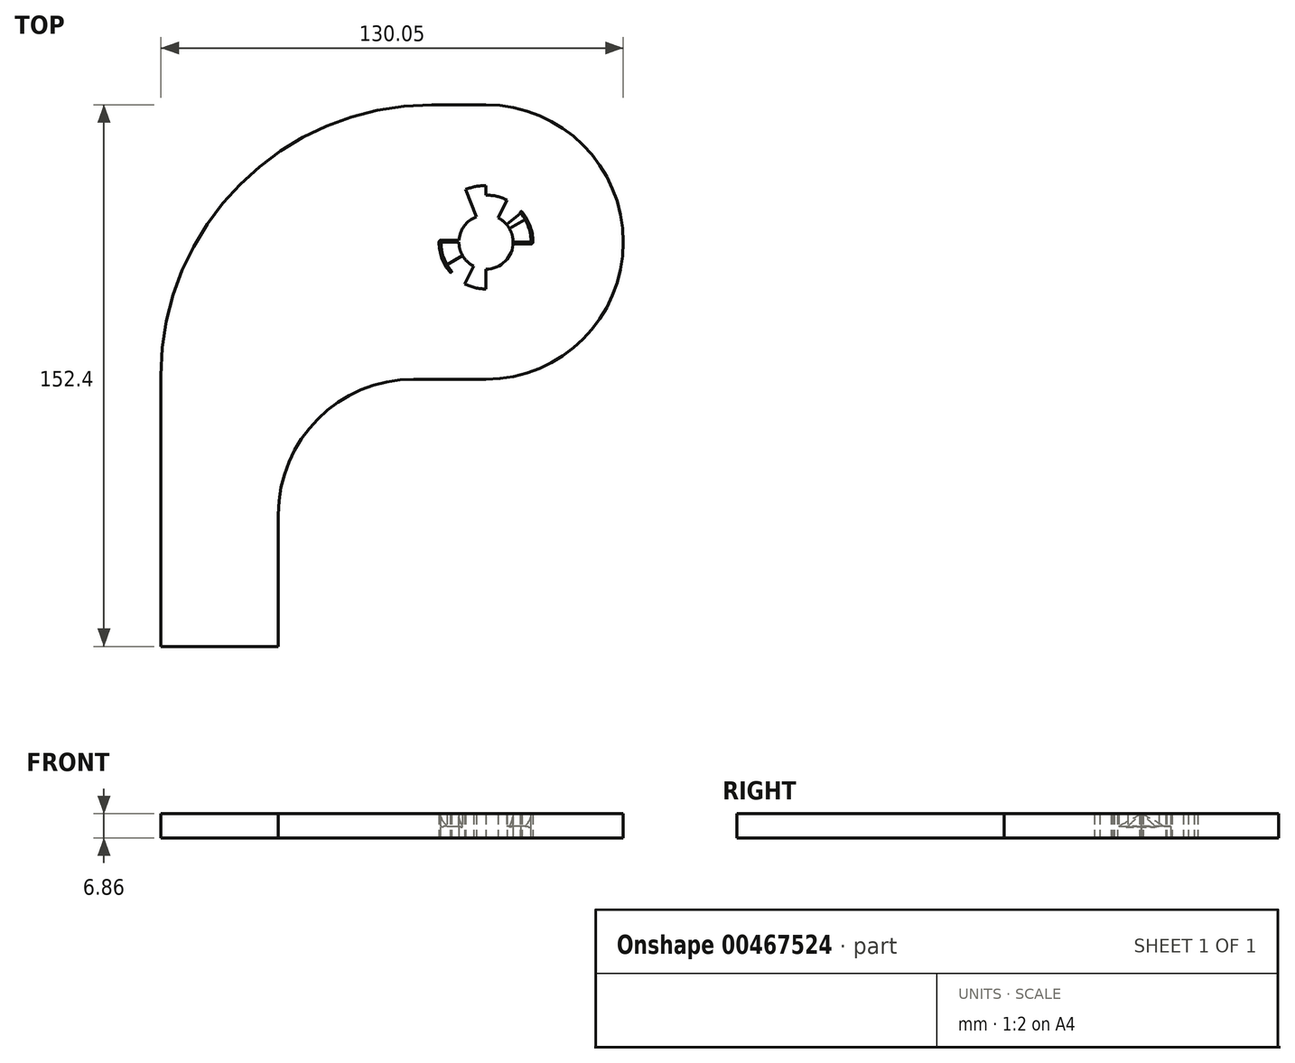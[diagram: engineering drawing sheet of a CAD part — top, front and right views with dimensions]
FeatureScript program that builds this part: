
annotation { "Feature Type Name" : "Feature", "Feature Type Description" : "" }
export const myFeature = defineFeature(function(context is Context, id is Id, definition is map)
    precondition{}
    {
        {
            var Q0;
            Q0=qCreatedBy(makeId("Front.planeOp"),FACE);
            var sketch = newSketch(context, id + "F0", { "sketchPlane" : qUnion([Q0])});
            skLineSegment(sketch, "E0", {"start": v(0, 0) * mm, "end": v(0, 25.4) * mm, "construction": true});
            skSolve(sketch);
        }
        {
            var Q0;
            Q0=qCreatedBy(makeId("Front.planeOp"),FACE);
            var Q1;
            Q1=sQuery(id+"F0.wireOp",EDGE,"E0");
            cPlane(context, id + "F1", {"entities" : qUnion([Q0, Q1]), "cplaneType" : CPlaneType.LINE_ANGLE, "offset" : 25.4 * mm, "angle" : 10 * degree, "width" : 152.4 * mm, "height" : 152.4 * mm});
        }
        {
            var Q0;
            Q0=qCreatedBy(makeId("Front.planeOp"),FACE);
            var Q1;
            Q1=sQuery(id+"F0.wireOp",EDGE,"E0");
            cPlane(context, id + "F2", {"entities" : qUnion([Q0, Q1]), "cplaneType" : CPlaneType.LINE_ANGLE, "offset" : 25.4 * mm, "angle" : 20 * degree, "width" : 152.4 * mm, "height" : 152.4 * mm});
        }
        {
            var Q0;
            Q0=qCreatedBy(makeId("Front.planeOp"),FACE);
            var Q1;
            Q1=sQuery(id+"F0.wireOp",EDGE,"E0");
            cPlane(context, id + "F3", {"entities" : qUnion([Q0, Q1]), "cplaneType" : CPlaneType.LINE_ANGLE, "offset" : 25.4 * mm, "angle" : 30 * degree, "width" : 152.4 * mm, "height" : 152.4 * mm});
        }
        {
            var Q0;
            Q0=qCreatedBy(makeId("Front.planeOp"),FACE);
            var sketch = newSketch(context, id + "F4", { "sketchPlane" : qUnion([Q0])});
            skLineSegment(sketch, "E1", {"start": v(0, 0) * mm, "end": v(-12.7, 0) * mm, "construction": true});
            skLineSegment(sketch, "E2.bottom", {"start": v(-12.7, 0) * mm, "end": v(-7.62, 0) * mm});
            skLineSegment(sketch, "E2.top", {"start": v(-12.7, 3.76) * mm, "end": v(-7.62, 3.76) * mm});
            skLineSegment(sketch, "E2.left", {"start": v(-12.7, 0) * mm, "end": v(-12.7, 3.76) * mm});
            skLineSegment(sketch, "E2.right", {"start": v(-7.62, 0) * mm, "end": v(-7.62, 3.76) * mm});
            skSolve(sketch);
        }
        {
            var Q0;
            Q0=qCreatedBy(id+"F1.planeOp",FACE);
            var sketch = newSketch(context, id + "F5", { "sketchPlane" : qUnion([Q0])});
            skLineSegment(sketch, "E3", {"start": v(0, 0) * mm, "end": v(12.7, 0) * mm, "construction": true});
            skLineSegment(sketch, "E4.bottom", {"start": v(12.7, 0) * mm, "end": v(7.62, 0) * mm});
            skLineSegment(sketch, "E4.top", {"start": v(12.7, 2.6) * mm, "end": v(7.62, 2.6) * mm});
            skLineSegment(sketch, "E4.left", {"start": v(12.7, 0) * mm, "end": v(12.7, 2.6) * mm});
            skLineSegment(sketch, "E4.right", {"start": v(7.62, 0) * mm, "end": v(7.62, 2.6) * mm});
            skSolve(sketch);
        }
        {
            var Q0;
            Q0=qCreatedBy(id+"F2.planeOp",FACE);
            var sketch = newSketch(context, id + "F6", { "sketchPlane" : qUnion([Q0])});
            skLineSegment(sketch, "E5", {"start": v(0, 0) * mm, "end": v(12.7, 0) * mm, "construction": true});
            skLineSegment(sketch, "E6.bottom", {"start": v(12.7, 0) * mm, "end": v(7.62, 0) * mm});
            skLineSegment(sketch, "E6.top", {"start": v(12.7, 1.42) * mm, "end": v(7.62, 1.42) * mm});
            skLineSegment(sketch, "E6.left", {"start": v(12.7, 0) * mm, "end": v(12.7, 1.42) * mm});
            skLineSegment(sketch, "E6.right", {"start": v(7.62, 0) * mm, "end": v(7.62, 1.42) * mm});
            skSolve(sketch);
        }
        {
            var Q0;
            Q0=qCreatedBy(id+"F3.planeOp",FACE);
            var sketch = newSketch(context, id + "F7", { "sketchPlane" : qUnion([Q0])});
            skLineSegment(sketch, "E7", {"start": v(0, 0) * mm, "end": v(12.7, 0) * mm, "construction": true});
            skLineSegment(sketch, "E8.bottom", {"start": v(12.7, 0) * mm, "end": v(7.62, 0) * mm});
            skLineSegment(sketch, "E8.top", {"start": v(12.7, 0.25) * mm, "end": v(7.62, 0.25) * mm});
            skLineSegment(sketch, "E8.left", {"start": v(12.7, 0) * mm, "end": v(12.7, 0.25) * mm});
            skLineSegment(sketch, "E8.right", {"start": v(7.62, 0) * mm, "end": v(7.62, 0.25) * mm});
            skLineSegment(sketch, "E9", {"start": v(0, 0) * mm, "end": v(-12.7, 0) * mm, "construction": true});
            skLineSegment(sketch, "E10.bottom", {"start": v(-12.7, 0) * mm, "end": v(-7.62, 0) * mm});
            skLineSegment(sketch, "E10.top", {"start": v(-12.7, 0.25) * mm, "end": v(-7.62, 0.25) * mm});
            skLineSegment(sketch, "E10.left", {"start": v(-12.7, 0) * mm, "end": v(-12.7, 0.25) * mm});
            skLineSegment(sketch, "E10.right", {"start": v(-7.62, 0) * mm, "end": v(-7.62, 0.25) * mm});
            skSolve(sketch);
        }
        {
            var Q0;
            Q0=makeQuery(id+"F7.imprint","IMPRINT",FACE,{"disambiguationData":[TD([[makeQuery(id+"F7.imprint","IMPRINT",EDGE,{"derivedFrom":sQuery(id+"F7.wireOp",EDGE,"E8.bottom")}),-1.0]])]});
            var Q1;
            Q1=makeQuery(id+"F6.imprint","IMPRINT",FACE,{"disambiguationData":[TD([[makeQuery(id+"F6.imprint","IMPRINT",EDGE,{"derivedFrom":sQuery(id+"F6.wireOp",EDGE,"E6.bottom")}),-1.0]])]});
            var Q2;
            Q2=makeQuery(id+"F5.imprint","IMPRINT",FACE,{"disambiguationData":[TD([[makeQuery(id+"F5.imprint","IMPRINT",EDGE,{"derivedFrom":sQuery(id+"F5.wireOp",EDGE,"E4.bottom")}),-1.0]])]});
            var Q3;
            Q3=makeQuery(id+"F4.imprint","IMPRINT",FACE,{"disambiguationData":[TD([[makeQuery(id+"F4.imprint","IMPRINT",EDGE,{"derivedFrom":sQuery(id+"F4.wireOp",EDGE,"E2.bottom")}),1.0]])]});
            loft(context, id + "F8", {"sheetProfilesArray" : [{ "sheetProfileEntities" : qUnion([Q0]) }, { "sheetProfileEntities" : qUnion([Q1]) }, { "sheetProfileEntities" : qUnion([Q2]) }, { "sheetProfileEntities" : qUnion([Q3]) }]});
        }
        {
            var Q0;
            Q0=qCreatedBy(id+"F2.planeOp",FACE);
            var sketch = newSketch(context, id + "F9", { "sketchPlane" : qUnion([Q0])});
            skLineSegment(sketch, "E11", {"start": v(0, 0) * mm, "end": v(-12.7, 0) * mm, "construction": true});
            skLineSegment(sketch, "E12.bottom", {"start": v(-12.7, 0) * mm, "end": v(-7.62, 0) * mm});
            skLineSegment(sketch, "E12.top", {"start": v(-12.7, 1.42) * mm, "end": v(-7.62, 1.42) * mm});
            skLineSegment(sketch, "E12.left", {"start": v(-12.7, 0) * mm, "end": v(-12.7, 1.42) * mm});
            skLineSegment(sketch, "E12.right", {"start": v(-7.62, 0) * mm, "end": v(-7.62, 1.42) * mm});
            skSolve(sketch);
        }
        {
            var Q0;
            Q0=qCreatedBy(id+"F1.planeOp",FACE);
            var sketch = newSketch(context, id + "F10", { "sketchPlane" : qUnion([Q0])});
            skLineSegment(sketch, "E13", {"start": v(0, 0) * mm, "end": v(-12.7, 0) * mm, "construction": true});
            skLineSegment(sketch, "E14.bottom", {"start": v(-12.7, 0) * mm, "end": v(-7.62, 0) * mm});
            skLineSegment(sketch, "E14.top", {"start": v(-12.7, 2.6) * mm, "end": v(-7.62, 2.6) * mm});
            skLineSegment(sketch, "E14.left", {"start": v(-12.7, 0) * mm, "end": v(-12.7, 2.6) * mm});
            skLineSegment(sketch, "E14.right", {"start": v(-7.62, 0) * mm, "end": v(-7.62, 2.6) * mm});
            skSolve(sketch);
        }
        {
            var Q0;
            Q0=qCreatedBy(makeId("Front.planeOp"),FACE);
            var sketch = newSketch(context, id + "F11", { "sketchPlane" : qUnion([Q0])});
            skLineSegment(sketch, "E15", {"start": v(0, 0) * mm, "end": v(12.7, 0) * mm, "construction": true});
            skLineSegment(sketch, "E16.bottom", {"start": v(12.7, 0) * mm, "end": v(7.62, 0) * mm});
            skLineSegment(sketch, "E16.top", {"start": v(12.7, 3.76) * mm, "end": v(7.62, 3.76) * mm});
            skLineSegment(sketch, "E16.left", {"start": v(12.7, 0) * mm, "end": v(12.7, 3.76) * mm});
            skLineSegment(sketch, "E16.right", {"start": v(7.62, 0) * mm, "end": v(7.62, 3.76) * mm});
            skSolve(sketch);
        }
        {
            var Q0;
            Q0=makeQuery(id+"F7.imprint","IMPRINT",FACE,{"disambiguationData":[TD([[makeQuery(id+"F7.imprint","IMPRINT",EDGE,{"derivedFrom":sQuery(id+"F7.wireOp",EDGE,"E10.bottom")}),1.0]])]});
            var Q1;
            Q1=makeQuery(id+"F9.imprint","IMPRINT",FACE,{"disambiguationData":[TD([[makeQuery(id+"F9.imprint","IMPRINT",EDGE,{"derivedFrom":sQuery(id+"F9.wireOp",EDGE,"E12.bottom")}),1.0]])]});
            var Q2;
            Q2=makeQuery(id+"F10.imprint","IMPRINT",FACE,{"disambiguationData":[TD([[makeQuery(id+"F10.imprint","IMPRINT",EDGE,{"derivedFrom":sQuery(id+"F10.wireOp",EDGE,"E14.bottom")}),1.0]])]});
            var Q3;
            Q3=makeQuery(id+"F11.imprint","IMPRINT",FACE,{"disambiguationData":[TD([[makeQuery(id+"F11.imprint","IMPRINT",EDGE,{"derivedFrom":sQuery(id+"F11.wireOp",EDGE,"E16.bottom")}),-1.0]])]});
            loft(context, id + "F12", {"sheetProfilesArray" : [{ "sheetProfileEntities" : qUnion([Q0]) }, { "sheetProfileEntities" : qUnion([Q1]) }, { "sheetProfileEntities" : qUnion([Q2]) }, { "sheetProfileEntities" : qUnion([Q3]) }]});
        }
        {
            var Q0;
            Q0=qCreatedBy(makeId("Top.planeOp"),FACE);
            var sketch = newSketch(context, id + "F13", { "sketchPlane" : qUnion([Q0])});
            skCircle(sketch, "E17", {"center": v(0, 0) * mm, "radius": 7.62 * mm, "construction": true});
            skLineSegment(sketch, "E18", {"start": v(0, 0) * mm, "end": v(13.08, -1.84) * mm, "construction": true});
            skLineSegment(sketch, "E19", {"start": v(0, 0) * mm, "end": v(-13.08, 1.84) * mm, "construction": true});
            skLineSegment(sketch, "E20", {"start": v(0, 0) * mm, "end": v(11.44, 6.6) * mm, "construction": true});
            skLineSegment(sketch, "E21", {"start": v(0, 0) * mm, "end": v(-11.44, -6.6) * mm, "construction": true});
            skArc(sketch, "E22", {"start": v(-7.62, 0) * mm, "mid": v(-2.22, 7.3) * mm, "end": v(6.33, 4.24) * mm});
            skArc(sketch, "E23", {"start": v(-6.33, -4.24) * mm, "mid": v(2.22, -7.3) * mm, "end": v(7.62, 0) * mm});
            skLineSegment(sketch, "E24", {"start": v(13.2, 0) * mm, "end": v(32.26, 0) * mm, "construction": true});
            skLineSegment(sketch, "E25", {"start": v(0, 13.2) * mm, "end": v(0, 38.6) * mm, "construction": true});
            skLineSegment(sketch, "E26", {"start": v(0, -13.2) * mm, "end": v(0, -38.6) * mm, "construction": true});
            skPoint(sketch, "E27.visualSharp", {"position": v(-91.44, -38.6) * mm});
            skPoint(sketch, "E28.visualSharp", {"position": v(-66.04, 38.6) * mm});
            skArc(sketch, "E29", {"start": v(12.7, 0) * mm, "mid": v(12.27, 3.29) * mm, "end": v(11, 6.35) * mm});
            skLineSegment(sketch, "E30", {"start": v(-11, -6.35) * mm, "end": v(-6.6, -3.8) * mm});
            skLineSegment(sketch, "E31", {"start": v(11, 6.35) * mm, "end": v(6.6, 3.81) * mm});
            skArc(sketch, "E32", {"start": v(6.6, 3.81) * mm, "mid": v(6.47, 4.03) * mm, "end": v(6.33, 4.24) * mm});
            skArc(sketch, "E33", {"start": v(-6.33, -4.24) * mm, "mid": v(-6.47, -4.03) * mm, "end": v(-6.6, -3.81) * mm});
            skCircle(sketch, "E34", {"center": v(0, 0) * mm, "radius": 7.62 * mm});
            skLineSegment(sketch, "E35.0", {"start": v(12.7, -0.5) * mm, "end": v(7.62, -0.5) * mm, "construction": true});
            skLineSegment(sketch, "E36.0", {"start": v(-12.7, 0.5) * mm, "end": v(-7.62, 0.5) * mm, "construction": true});
            skLineSegment(sketch, "E37", {"start": v(0, 0) * mm, "end": v(-13.45, -11.28) * mm, "construction": true});
            skLineSegment(sketch, "E38", {"start": v(0, 0) * mm, "end": v(13.65, 11.45) * mm});
            skArc(sketch, "E39.0", {"start": v(-13.2, 0) * mm, "mid": v(-12.76, -3.42) * mm, "end": v(-11.44, -6.6) * mm});
            skArc(sketch, "E40.0", {"start": v(13.2, 0) * mm, "mid": v(12.76, 3.42) * mm, "end": v(11.44, 6.6) * mm});
            skArc(sketch, "E41", {"start": v(-13.2, 0) * mm, "mid": v(-12.41, -4.52) * mm, "end": v(-10.12, -8.49) * mm});
            skArc(sketch, "E42", {"start": v(13.2, 0) * mm, "mid": v(12.41, 4.52) * mm, "end": v(10.12, 8.49) * mm});
            skLineSegment(sketch, "E43", {"start": v(-12.7, 0.5) * mm, "end": v(-7.62, 0.5) * mm});
            skLineSegment(sketch, "E44", {"start": v(7.62, -0.5) * mm, "end": v(12.7, -0.5) * mm});
            skArc(sketch, "E45", {"start": v(-12.7, 0.5) * mm, "mid": v(-13.06, 0.36) * mm, "end": v(-13.2, 0) * mm});
            skArc(sketch, "E46", {"start": v(12.7, -0.5) * mm, "mid": v(13.06, -0.36) * mm, "end": v(13.2, 0) * mm});
            skArc(sketch, "E47", {"start": v(11, 6.35) * mm, "mid": v(10.4, 7.28) * mm, "end": v(9.73, 8.16) * mm});
            skArc(sketch, "E48", {"start": v(10.12, 8.49) * mm, "mid": v(9.76, 8.52) * mm, "end": v(9.73, 8.16) * mm});
            skArc(sketch, "E49", {"start": v(-10.12, -8.49) * mm, "mid": v(-9.77, -8.5) * mm, "end": v(-9.73, -8.16) * mm});
            skLineSegment(sketch, "E50", {"start": v(12.7, 0) * mm, "end": v(7.62, 0) * mm});
            skArc(sketch, "E51", {"start": v(7.62, -0.5) * mm, "mid": v(7.63, -0.25) * mm, "end": v(7.64, 0) * mm});
            skArc(sketch, "E52", {"start": v(-9.73, -8.16) * mm, "mid": v(-11.93, -4.34) * mm, "end": v(-12.7, 0) * mm});
            skLineSegment(sketch, "E53", {"start": v(-12.7, 0) * mm, "end": v(-7.62, 0) * mm});
            skLineSegment(sketch, "E54", {"start": v(-7.62, 0.5) * mm, "end": v(-7.6, 0.5) * mm});
            skArc(sketch, "E55", {"start": v(-7.62, 0) * mm, "mid": v(-7.62, 0.25) * mm, "end": v(-7.6, 0.5) * mm});
            skLineSegment(sketch, "E56", {"start": v(0, 0) * mm, "end": v(8.65, 16.97) * mm, "construction": true});
            skLineSegment(sketch, "E57", {"start": v(0, 0) * mm, "end": v(-8.65, -16.97) * mm, "construction": true});
            skCircle(sketch, "E58", {"center": v(0, 0) * mm, "radius": 13.2 * mm, "construction": true});
            skLineSegment(sketch, "E59", {"start": v(0, 0) * mm, "end": v(0, 19.05) * mm, "construction": true});
            skLineSegment(sketch, "E60", {"start": v(0, 0) * mm, "end": v(0, -19.05) * mm, "construction": true});
            skArc(sketch, "E61", {"start": v(0, 13.2) * mm, "mid": v(3.08, 12.84) * mm, "end": v(6, 11.77) * mm});
            skArc(sketch, "E62", {"start": v(-6, -11.77) * mm, "mid": v(-3.08, -12.84) * mm, "end": v(0, -13.2) * mm});
            skLineSegment(sketch, "E63", {"start": v(0, 7.62) * mm, "end": v(0, 13.2) * mm});
            skLineSegment(sketch, "E64", {"start": v(6, 11.77) * mm, "end": v(3.46, 6.79) * mm});
            skLineSegment(sketch, "E65", {"start": v(3.46, 6.79) * mm, "end": v(-6, -11.77) * mm});
            skLineSegment(sketch, "E66", {"start": v(0, -13.2) * mm, "end": v(0, -7.62) * mm});
            skLineSegment(sketch, "E67", {"start": v(0, 0) * mm, "end": v(7.72, -20.12) * mm, "construction": true});
            skCircle(sketch, "E68", {"center": v(0, 0) * mm, "radius": 15.88 * mm, "construction": true});
            skLineSegment(sketch, "E69", {"start": v(2.73, -7.11) * mm, "end": v(5.69, -14.82) * mm, "construction": true});
            skArc(sketch, "E70", {"start": v(0, -15.88) * mm, "mid": v(2.9, -15.6) * mm, "end": v(5.69, -14.82) * mm});
            skLineSegment(sketch, "E71", {"start": v(5.69, -14.82) * mm, "end": v(2.73, -7.11) * mm});
            skLineSegment(sketch, "E72", {"start": v(0, 0) * mm, "end": v(-5.69, 14.82) * mm, "construction": true});
            skArc(sketch, "E73", {"start": v(-5.69, 14.82) * mm, "mid": v(-2.9, 15.6) * mm, "end": v(0, 15.87) * mm});
            skLineSegment(sketch, "E74", {"start": v(-5.69, 14.82) * mm, "end": v(-2.73, 7.11) * mm});
            skLineSegment(sketch, "E75", {"start": v(0, 15.87) * mm, "end": v(0, 7.62) * mm});
            skArc(sketch, "E76", {"start": v(2.73, -7.11) * mm, "mid": v(1.39, -7.5) * mm, "end": v(0, -7.62) * mm});
            skLineSegment(sketch, "E77", {"start": v(0, -13.2) * mm, "end": v(0, -15.88) * mm});
            skPoint(sketch, "E78.visualSharp", {"position": v(91.44, 38.6) * mm});
            skArc(sketch, "E79.MirrorCS", {"start": v(0, 38.6) * mm, "mid": v(38.6, 0) * mm, "end": v(0, -38.6) * mm});
            skArc(sketch, "E80.MirrorCS", {"start": v(-58.42, -76.7) * mm, "mid": v(-47.26, -49.77) * mm, "end": v(-20.32, -38.6) * mm});
            skLineSegment(sketch, "E81.MirrorCS", {"start": v(-58.42, -113.8) * mm, "end": v(-58.42, -76.7) * mm});
            skLineSegment(sketch, "E82.MirrorCS", {"start": v(-91.44, -113.8) * mm, "end": v(-58.42, -113.8) * mm});
            skLineSegment(sketch, "E83.MirrorCS", {"start": v(-91.44, -37.6) * mm, "end": v(-91.44, -113.8) * mm});
            skArc(sketch, "E84.MirrorCS", {"start": v(-91.44, -37.6) * mm, "mid": v(-69.12, 16.29) * mm, "end": v(-15.24, 38.6) * mm});
            skLineSegment(sketch, "E85.MirrorCS", {"start": v(0, 38.6) * mm, "end": v(-15.24, 38.6) * mm});
            skLineSegment(sketch, "E86.MirrorCS", {"start": v(-20.32, -38.6) * mm, "end": v(0, -38.6) * mm});
            skSolve(sketch);
        }
        {
            var Q0;
            {var subQ1=sQuery(id+"F13.wireOp",EDGE,"E66");Q0=makeQuery(id+"F13.imprint","IMPRINT",FACE,{"disambiguationData":[TD([[makeQuery(id+"F13.imprint","IMPRINT",EDGE,{"derivedFrom":subQ1}),-1.0]])]});}
            var Q1;
            {var subQ1=sQuery(id+"F13.wireOp",EDGE,"E73");Q1=makeQuery(id+"F13.imprint","IMPRINT",FACE,{"disambiguationData":[TD([[makeQuery(id+"F13.imprint","IMPRINT",EDGE,{"derivedFrom":subQ1}),-1.0]])]});}
            extrude(context, id + "F14", {"entities" : qUnion([Q0, Q1]), "operationType" : NewBodyOperationType.ADD, "depth" : 3.8 * mm});
        }
        {
            var Q0;
            {var subQ3=sQuery(id+"F13.wireOp",EDGE,"E30");Q0=makeQuery(id+"F13.imprint","IMPRINT",FACE,{"disambiguationData":[TD([[makeQuery(id+"F13.imprint","IMPRINT",EDGE,{"derivedFrom":subQ3}),-1.0]])]});}
            var Q1;
            {var subQ0=sQuery(id+"F13.wireOp",EDGE,"E31");Q1=makeQuery(id+"F13.imprint","IMPRINT",FACE,{"disambiguationData":[TD([[makeQuery(id+"F13.imprint","IMPRINT",EDGE,{"derivedFrom":subQ0}),-1.0]])]});}
            var Q2;
            {var subQ1=sQuery(id+"F13.wireOp",EDGE,"E29");Q2=makeQuery(id+"F13.imprint","IMPRINT",FACE,{"disambiguationData":[TD([[makeQuery(id+"F13.imprint","IMPRINT",EDGE,{"derivedFrom":subQ1}),1.0]])]});}
            var Q3;
            {var subQ0=sQuery(id+"F13.wireOp",EDGE,"E30");Q3=makeQuery(id+"F13.imprint","IMPRINT",FACE,{"disambiguationData":[TD([[makeQuery(id+"F13.imprint","IMPRINT",EDGE,{"derivedFrom":subQ0}),1.0]])]});}
            var Q4;
            {var subQ1=sQuery(id+"F13.wireOp",EDGE,"E73");Q4=makeQuery(id+"F13.imprint","IMPRINT",FACE,{"disambiguationData":[TD([[makeQuery(id+"F13.imprint","IMPRINT",EDGE,{"derivedFrom":subQ1}),-1.0]])]});}
            var Q5;
            {var subQ1=sQuery(id+"F13.wireOp",EDGE,"E66");Q5=makeQuery(id+"F13.imprint","IMPRINT",FACE,{"disambiguationData":[TD([[makeQuery(id+"F13.imprint","IMPRINT",EDGE,{"derivedFrom":subQ1}),-1.0]])]});}
            extrude(context, id + "F15", {"entities" : qUnion([Q0, Q1, Q2, Q3, Q4, Q5]), "depth" : 0.25 * mm});
        }
        {
            var Q0;
            Q0=makeQuery(id+"F15.opExtrude","CAP_FACE",FACE,{"disambiguationData":[OSD([sQuery(id+"F13.wireOp",EDGE,"E29"),sQuery(id+"F13.wireOp",EDGE,"E34"),sQuery(id+"F13.wireOp",EDGE,"E41"),sQuery(id+"F13.wireOp",EDGE,"E42"),sQuery(id+"F13.wireOp",EDGE,"E43"),sQuery(id+"F13.wireOp",EDGE,"E44"),sQuery(id+"F13.wireOp",EDGE,"E45"),sQuery(id+"F13.wireOp",EDGE,"E46"),sQuery(id+"F13.wireOp",EDGE,"E47"),sQuery(id+"F13.wireOp",EDGE,"E48"),sQuery(id+"F13.wireOp",EDGE,"E49"),sQuery(id+"F13.wireOp",EDGE,"E50"),sQuery(id+"F13.wireOp",EDGE,"E51"),sQuery(id+"F13.wireOp",EDGE,"E52"),sQuery(id+"F13.wireOp",EDGE,"E53"),sQuery(id+"F13.wireOp",EDGE,"E54"),sQuery(id+"F13.wireOp",EDGE,"E61"),sQuery(id+"F13.wireOp",EDGE,"E62"),sQuery(id+"F13.wireOp",EDGE,"E64"),sQuery(id+"F13.wireOp",EDGE,"E65"),sQuery(id+"F13.wireOp",EDGE,"E66"),sQuery(id+"F13.wireOp",EDGE,"E75"),sQuery(id+"F13.wireOp",EDGE,"c743eb21-dba2-4873-9057-679fcddca16c0.MirrorCS"),sQuery(id+"F13.wireOp",EDGE,"qGRwGEuw-6LeP-Z8Zf-1Xi4-EfhECfa87SC8"),sQuery(id+"F13.wireOp",EDGE,"y9YU23Bv-ha3m-shEu-oYII-tfs9zsREy9GK"),sQuery(id+"F13.wireOp",EDGE,"las0jonK-rq68-rycF-1vXh-9Th4UhI6eniF"),sQuery(id+"F13.wireOp",EDGE,"HExbY8bb-ckJ1-AvVd-cz2N-ByrrFEVJddwJ"),sQuery(id+"F13.wireOp",EDGE,"Ix7P7fZl-JRkV-YXA1-5Ihu-swie9BlHH8H5"),sQuery(id+"F13.wireOp",EDGE,"E78.filletArc"),sQuery(id+"F13.wireOp",EDGE,"fb1370dd-7f9d-4dee-a025-498a89b70b72.filletArc")])],"isStart":true});
            extrude(context, id + "F16", {"entities" : qUnion([Q0]), "depth" : 3.05 * mm});
        }
        {
            var Q0;
            {var subQ1=sQuery(id+"F13.wireOp",EDGE,"E66");Q0=makeQuery(id+"F13.imprint","IMPRINT",FACE,{"disambiguationData":[TD([[makeQuery(id+"F13.imprint","IMPRINT",EDGE,{"derivedFrom":subQ1}),-1.0]])]});}
            var Q1;
            {var subQ1=sQuery(id+"F13.wireOp",EDGE,"E73");Q1=makeQuery(id+"F13.imprint","IMPRINT",FACE,{"disambiguationData":[TD([[makeQuery(id+"F13.imprint","IMPRINT",EDGE,{"derivedFrom":subQ1}),-1.0]])]});}
            extrude(context, id + "F17", {"entities" : qUnion([Q0, Q1]), "operationType" : NewBodyOperationType.ADD, "depth" : 3.8 * mm});
        }
    });
